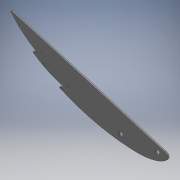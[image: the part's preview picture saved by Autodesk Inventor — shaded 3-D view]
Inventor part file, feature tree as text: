
AUTODESK INVENTOR PART (.ipt)
format: ipt  version: 2018 (Build 220112000, 112)  size: 174,080 bytes
history: native  units: mm
features: projected_geometry x3, extrude x2, sketch x2, fillet x1
ambient origin geometry x8: Origin, YZ Plane, XZ Plane, XY Plane, X Axis, Y Axis, Z Axis, Center Point
bodies: Body1 (feature_tree)
feature tree (8):
  extrude  "押し出し2"  Depth=4.0mm TaperAngle=0.0deg
  fillet  "フィレット2"  Radius=3.0mm
  extrude  "押し出し3"  Depth=100.0mm
  sketch  "スケッチ2"
  projected_geometry  "投影ループ4"
  projected_geometry  "投影ループ5"
  projected_geometry  "投影ループ6"
  sketch  "スケッチ3"
